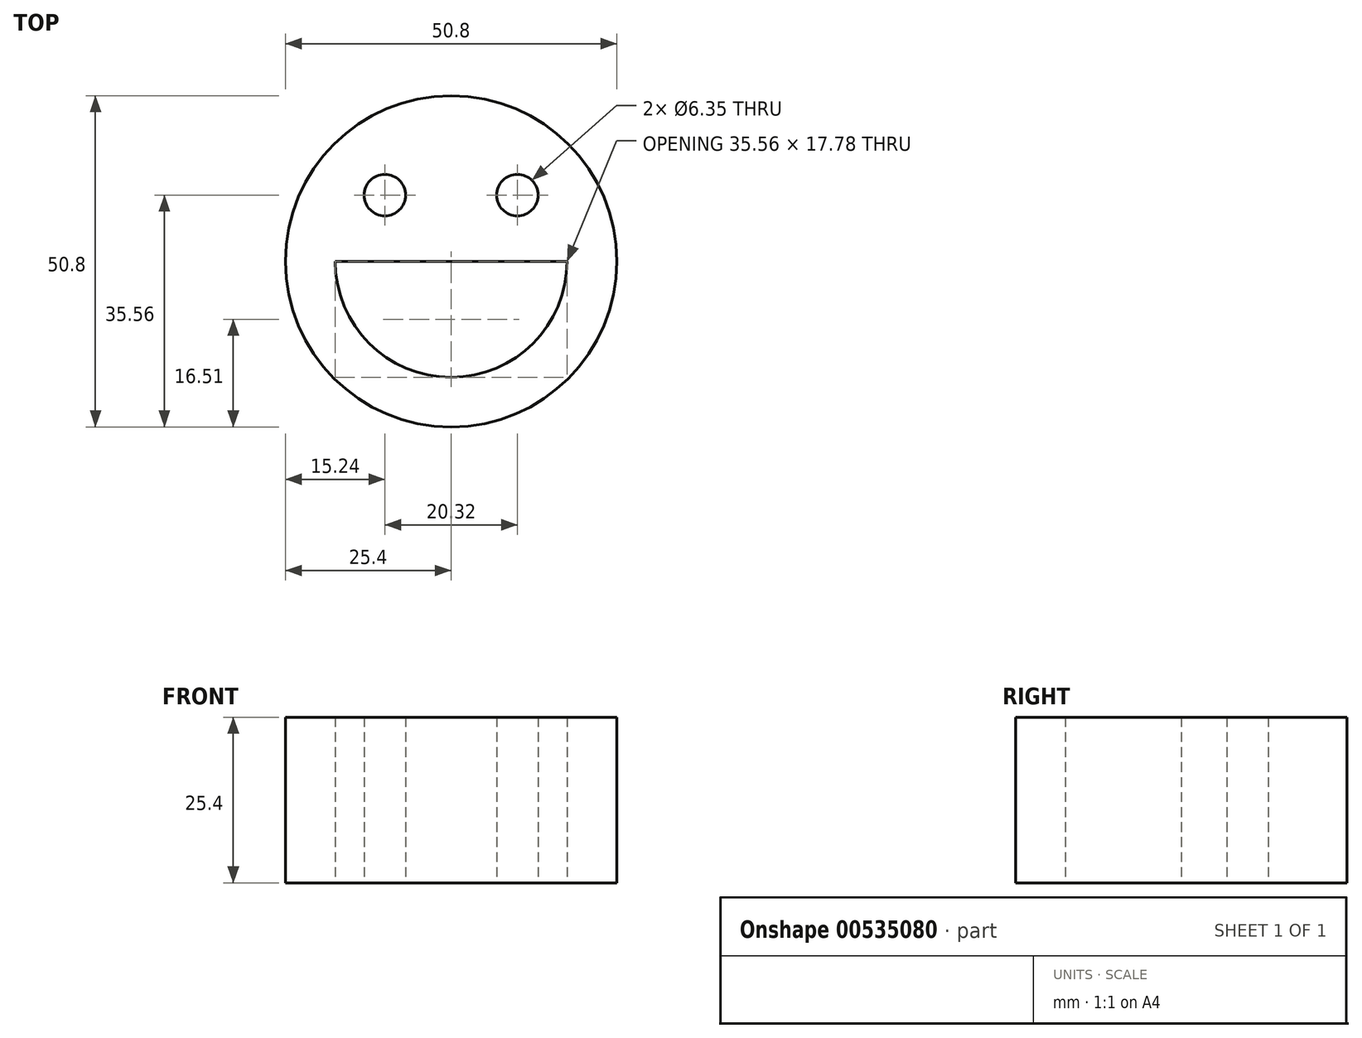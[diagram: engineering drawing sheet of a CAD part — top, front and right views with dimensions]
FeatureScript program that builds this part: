
annotation { "Feature Type Name" : "Feature", "Feature Type Description" : "" }
export const myFeature = defineFeature(function(context is Context, id is Id, definition is map)
    precondition{}
    {
        {
            var Q0;
            Q0=qCreatedBy(makeId("Top.planeOp"),FACE);
            var sketch = newSketch(context, id + "F0", { "sketchPlane" : qUnion([Q0])});
            skCircle(sketch, "E0", {"center": v(0, 0) * mm, "radius": 25.4 * mm});
            skCircle(sketch, "E1", {"center": v(-10.16, 10.16) * mm, "radius": 3.18 * mm});
            skCircle(sketch, "E2", {"center": v(10.16, 10.16) * mm, "radius": 3.18 * mm});
            skArc(sketch, "E3", {"start": v(17.78, 0) * mm, "mid": v(0, -17.78) * mm, "end": v(-17.78, 0) * mm});
            skLineSegment(sketch, "E4", {"start": v(-17.78, 0) * mm, "end": v(17.78, 0) * mm});
            skSolve(sketch);
        }
        {
            var Q0;
            Q0 = qSketchRegion(id + "F0", true);
            extrude(context, id + "F1", {"entities" : qUnion([Q0]), "depth" : 25.4 * mm, "offsetDistance" : 25.4 * mm});
        }
    });
